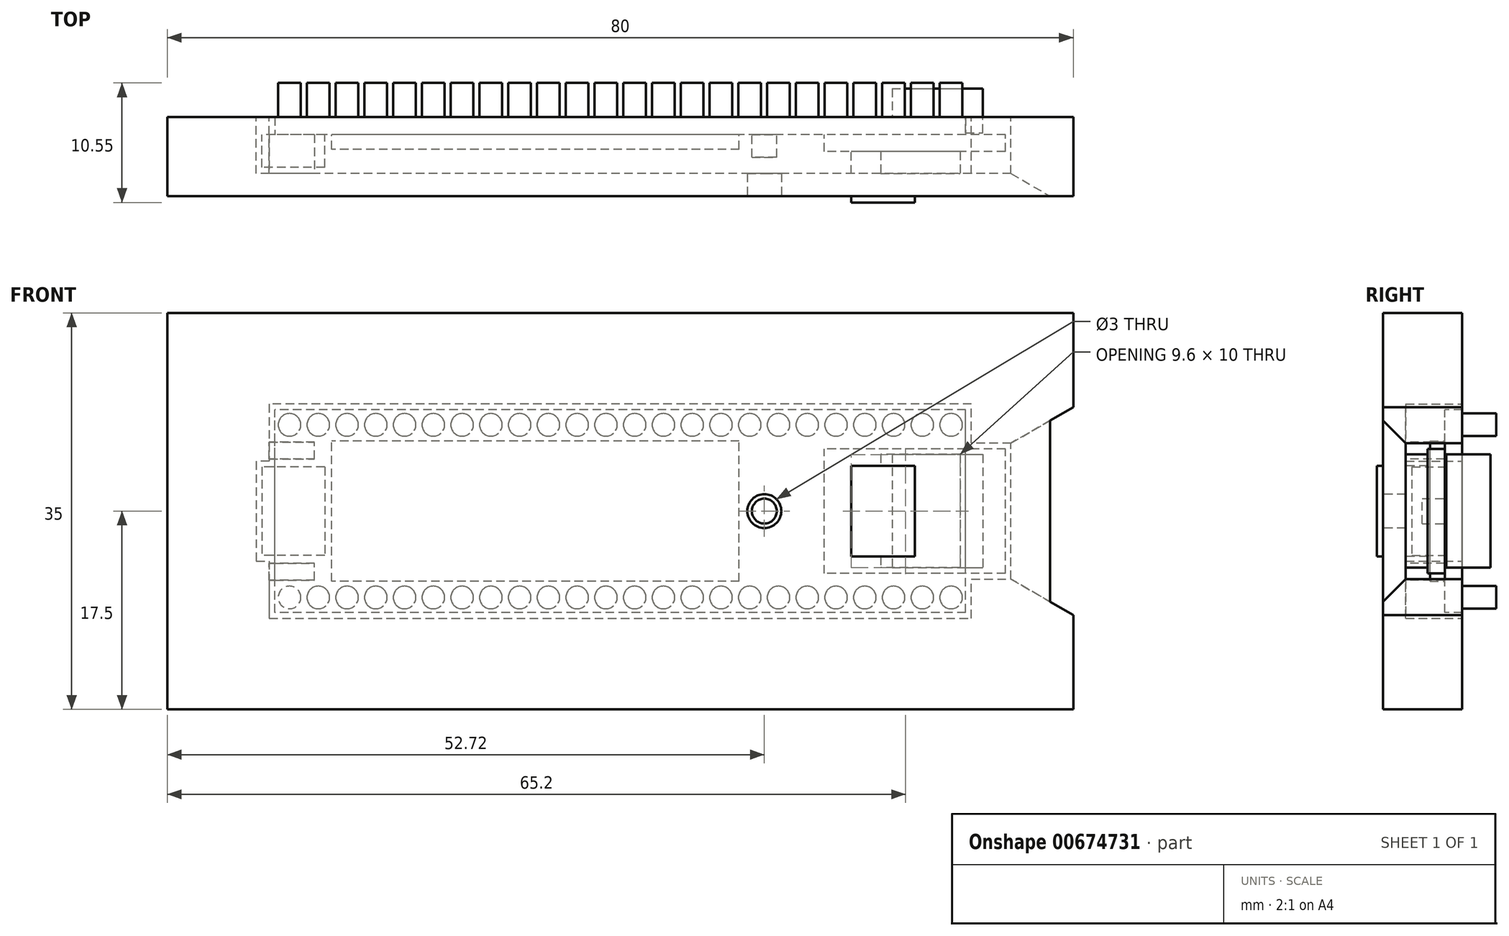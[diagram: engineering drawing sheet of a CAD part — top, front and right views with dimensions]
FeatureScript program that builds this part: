
annotation { "Feature Type Name" : "Feature", "Feature Type Description" : "" }
export const myFeature = defineFeature(function(context is Context, id is Id, definition is map)
    precondition{}
    {
        {
            var Q0;
            Q0=qCreatedBy(makeId("Front.planeOp"),FACE);
            var sketch = newSketch(context, id + "F0", { "sketchPlane" : qUnion([Q0])});
            skLineSegment(sketch, "E0.bottom", {"start": v(30.5, -8.95) * mm, "end": v(-30.5, -8.95) * mm});
            skLineSegment(sketch, "E0.top", {"start": v(30.5, 8.95) * mm, "end": v(-30.5, 8.95) * mm});
            skLineSegment(sketch, "E0.left", {"start": v(30.5, -8.95) * mm, "end": v(30.5, 8.95) * mm});
            skLineSegment(sketch, "E0.right", {"start": v(-30.5, -8.95) * mm, "end": v(-30.5, 8.95) * mm});
            skPoint(sketch, "E0.middle", {"position": v(0, 0) * mm});
            skCircle(sketch, "E1", {"center": v(12.72, 0) * mm, "radius": 1.1 * mm});
            skLineSegment(sketch, "E2.bottom", {"start": v(34, -5.5) * mm, "end": v(18, -5.5) * mm});
            skLineSegment(sketch, "E2.top", {"start": v(34, 5.5) * mm, "end": v(18, 5.5) * mm});
            skLineSegment(sketch, "E2.left", {"start": v(34, -5.5) * mm, "end": v(34, 5.5) * mm});
            skLineSegment(sketch, "E2.right", {"start": v(18, -5.5) * mm, "end": v(18, 5.5) * mm});
            skPoint(sketch, "E2.middle", {"position": v(26, 0) * mm});
            skLineSegment(sketch, "E3.bottom", {"start": v(-26.1, 3.9) * mm, "end": v(-31.65, 3.9) * mm});
            skLineSegment(sketch, "E3.top", {"start": v(-26.1, -3.9) * mm, "end": v(-31.65, -3.9) * mm});
            skLineSegment(sketch, "E3.left", {"start": v(-26.1, 3.9) * mm, "end": v(-26.1, -3.9) * mm});
            skLineSegment(sketch, "E3.right", {"start": v(-31.65, 3.9) * mm, "end": v(-31.65, -3.9) * mm});
            skPoint(sketch, "E3.middle", {"position": v(-28.87, 0) * mm});
            skLineSegment(sketch, "E4.bottom", {"start": v(10.5, -6.2) * mm, "end": v(-25.5, -6.2) * mm});
            skLineSegment(sketch, "E4.top", {"start": v(10.5, 6.2) * mm, "end": v(-25.5, 6.2) * mm});
            skLineSegment(sketch, "E4.left", {"start": v(10.5, -6.2) * mm, "end": v(10.5, 6.2) * mm});
            skLineSegment(sketch, "E4.right", {"start": v(-25.5, -6.2) * mm, "end": v(-25.5, 6.2) * mm});
            skPoint(sketch, "E4.middle", {"position": v(-7.5, 0) * mm});
            skSolve(sketch);
        }
        {
            var Q0;
            {var subQ8=sQuery(id+"F0.wireOp",EDGE,"E0.bottom");Q0=makeQuery(id+"F0.imprint","IMPRINT",FACE,{"disambiguationData":[TD([[makeQuery(id+"F0.imprint","IMPRINT",EDGE,{"derivedFrom":subQ8}),-1.0]])]});}
            var Q1;
            {var subQ5=sQuery(id+"F0.wireOp",EDGE,"E3.left");Q1=makeQuery(id+"F0.imprint","IMPRINT",FACE,{"disambiguationData":[TD([[makeQuery(id+"F0.imprint","IMPRINT",EDGE,{"derivedFrom":subQ5}),-1.0]])]});}
            var Q2;
            {var subQ5=sQuery(id+"F0.wireOp",EDGE,"E2.right");Q2=makeQuery(id+"F0.imprint","IMPRINT",FACE,{"disambiguationData":[TD([[makeQuery(id+"F0.imprint","IMPRINT",EDGE,{"derivedFrom":subQ5}),-1.0]])]});}
            var Q3;
            Q3=makeQuery(id+"F0.imprint","IMPRINT",FACE,{"disambiguationData":[TD([[makeQuery(id+"F0.imprint","IMPRINT",EDGE,{"derivedFrom":sQuery(id+"F0.wireOp",EDGE,"E1")}),1.0]])]});
            var Q4;
            Q4=makeQuery(id+"F0.imprint","IMPRINT",FACE,{"disambiguationData":[TD([[makeQuery(id+"F0.imprint","IMPRINT",EDGE,{"derivedFrom":sQuery(id+"F0.wireOp",EDGE,"E4.bottom")}),-1.0]])]});
            extrude(context, id + "F1", {"entities" : qUnion([Q0, Q1, Q2, Q3, Q4]), "oppositeDirection" : true, "depth" : 1.55 * mm, "offsetDistance" : 25 * mm});
        }
        {
            var Q0;
            Q0=makeQuery(id+"F0.imprint","IMPRINT",FACE,{"disambiguationData":[TD([[makeQuery(id+"F0.imprint","IMPRINT",EDGE,{"derivedFrom":sQuery(id+"F0.wireOp",EDGE,"E1")}),1.0]])]});
            extrude(context, id + "F2", {"entities" : qUnion([Q0]), "operationType" : NewBodyOperationType.ADD, "depth" : 2 * mm, "offsetDistance" : 25 * mm});
        }
        {
            var Q0;
            {var subQ5=sQuery(id+"F0.wireOp",EDGE,"E3.left");Q0=makeQuery(id+"F0.imprint","IMPRINT",FACE,{"disambiguationData":[TD([[makeQuery(id+"F0.imprint","IMPRINT",EDGE,{"derivedFrom":subQ5}),-1.0]])]});}
            var Q1;
            {var subQ5=sQuery(id+"F0.wireOp",EDGE,"E3.right");Q1=makeQuery(id+"F0.imprint","IMPRINT",FACE,{"disambiguationData":[TD([[makeQuery(id+"F0.imprint","IMPRINT",EDGE,{"derivedFrom":subQ5}),1.0]])]});}
            extrude(context, id + "F3", {"entities" : qUnion([Q0, Q1]), "operationType" : NewBodyOperationType.ADD, "depth" : 2.9 * mm, "offsetDistance" : 25 * mm});
        }
        {
            var Q0;
            {var subQ5=sQuery(id+"F0.wireOp",EDGE,"E2.left");Q0=makeQuery(id+"F0.imprint","IMPRINT",FACE,{"disambiguationData":[TD([[makeQuery(id+"F0.imprint","IMPRINT",EDGE,{"derivedFrom":subQ5}),1.0]])]});}
            var Q1;
            {var subQ5=sQuery(id+"F0.wireOp",EDGE,"E2.right");Q1=makeQuery(id+"F0.imprint","IMPRINT",FACE,{"disambiguationData":[TD([[makeQuery(id+"F0.imprint","IMPRINT",EDGE,{"derivedFrom":subQ5}),-1.0]])]});}
            extrude(context, id + "F4", {"entities" : qUnion([Q0, Q1]), "operationType" : NewBodyOperationType.ADD, "depth" : 1.5 * mm, "offsetDistance" : 25 * mm});
        }
        {
            var Q0;
            Q0=makeQuery(id+"F0.imprint","IMPRINT",FACE,{"disambiguationData":[TD([[makeQuery(id+"F0.imprint","IMPRINT",EDGE,{"derivedFrom":sQuery(id+"F0.wireOp",EDGE,"E4.bottom")}),-1.0]])]});
            extrude(context, id + "F5", {"entities" : qUnion([Q0]), "operationType" : NewBodyOperationType.ADD, "depth" : 1.3 * mm, "offsetDistance" : 25 * mm});
        }
        {
            var Q0;
            Q0=makeQuery(id+"F1.opExtrude","CAP_FACE",FACE,{"disambiguationData":[OSD([sQuery(id+"F0.wireOp",EDGE,"E0.bottom"),sQuery(id+"F0.wireOp",EDGE,"E0.top"),sQuery(id+"F0.wireOp",EDGE,"E0.left"),sQuery(id+"F0.wireOp",EDGE,"E0.right")])],"isStart":false});
            var sketch = newSketch(context, id + "F6", { "sketchPlane" : qUnion([Q0])});
            skCircle(sketch, "E5", {"center": v(29.21, -7.62) * mm, "radius": 1 * mm});
            skCircle(sketch, "E6.0.1.0", {"center": v(29.21, 7.62) * mm, "radius": 1 * mm});
            skCircle(sketch, "E6.1.0.0", {"center": v(26.67, -7.62) * mm, "radius": 1 * mm});
            skCircle(sketch, "E6.1.1.0", {"center": v(26.67, 7.62) * mm, "radius": 1 * mm});
            skCircle(sketch, "E6.2.0.0", {"center": v(24.13, -7.62) * mm, "radius": 1 * mm});
            skCircle(sketch, "E6.2.1.0", {"center": v(24.13, 7.62) * mm, "radius": 1 * mm});
            skCircle(sketch, "E6.3.0.0", {"center": v(21.6, -7.62) * mm, "radius": 1 * mm});
            skCircle(sketch, "E6.3.1.0", {"center": v(21.6, 7.62) * mm, "radius": 1 * mm});
            skCircle(sketch, "E6.4.0.0", {"center": v(19.05, -7.62) * mm, "radius": 1 * mm});
            skCircle(sketch, "E6.4.1.0", {"center": v(19.05, 7.62) * mm, "radius": 1 * mm});
            skCircle(sketch, "E6.5.0.0", {"center": v(16.51, -7.62) * mm, "radius": 1 * mm});
            skCircle(sketch, "E6.5.1.0", {"center": v(16.51, 7.62) * mm, "radius": 1 * mm});
            skCircle(sketch, "E6.6.0.0", {"center": v(13.97, -7.62) * mm, "radius": 1 * mm});
            skCircle(sketch, "E6.6.1.0", {"center": v(13.97, 7.62) * mm, "radius": 1 * mm});
            skCircle(sketch, "E6.7.0.0", {"center": v(11.43, -7.62) * mm, "radius": 1 * mm});
            skCircle(sketch, "E6.7.1.0", {"center": v(11.43, 7.62) * mm, "radius": 1 * mm});
            skCircle(sketch, "E6.8.0.0", {"center": v(8.9, -7.62) * mm, "radius": 1 * mm});
            skCircle(sketch, "E6.8.1.0", {"center": v(8.9, 7.62) * mm, "radius": 1 * mm});
            skCircle(sketch, "E6.9.0.0", {"center": v(6.35, -7.62) * mm, "radius": 1 * mm});
            skCircle(sketch, "E6.9.1.0", {"center": v(6.35, 7.62) * mm, "radius": 1 * mm});
            skCircle(sketch, "E6.10.0.0", {"center": v(3.81, -7.62) * mm, "radius": 1 * mm});
            skCircle(sketch, "E6.10.1.0", {"center": v(3.81, 7.62) * mm, "radius": 1 * mm});
            skCircle(sketch, "E6.11.0.0", {"center": v(1.27, -7.62) * mm, "radius": 1 * mm});
            skCircle(sketch, "E6.11.1.0", {"center": v(1.27, 7.62) * mm, "radius": 1 * mm});
            skCircle(sketch, "E6.12.0.0", {"center": v(-1.27, -7.62) * mm, "radius": 1 * mm});
            skCircle(sketch, "E6.12.1.0", {"center": v(-1.27, 7.62) * mm, "radius": 1 * mm});
            skCircle(sketch, "E6.13.0.0", {"center": v(-3.81, -7.62) * mm, "radius": 1 * mm});
            skCircle(sketch, "E6.13.1.0", {"center": v(-3.81, 7.62) * mm, "radius": 1 * mm});
            skCircle(sketch, "E6.14.0.0", {"center": v(-6.35, -7.62) * mm, "radius": 1 * mm});
            skCircle(sketch, "E6.14.1.0", {"center": v(-6.35, 7.62) * mm, "radius": 1 * mm});
            skCircle(sketch, "E6.15.0.0", {"center": v(-8.9, -7.62) * mm, "radius": 1 * mm});
            skCircle(sketch, "E6.15.1.0", {"center": v(-8.9, 7.62) * mm, "radius": 1 * mm});
            skCircle(sketch, "E6.16.0.0", {"center": v(-11.43, -7.62) * mm, "radius": 1 * mm});
            skCircle(sketch, "E6.16.1.0", {"center": v(-11.43, 7.62) * mm, "radius": 1 * mm});
            skCircle(sketch, "E6.17.0.0", {"center": v(-13.97, -7.62) * mm, "radius": 1 * mm});
            skCircle(sketch, "E6.17.1.0", {"center": v(-13.97, 7.62) * mm, "radius": 1 * mm});
            skCircle(sketch, "E6.18.0.0", {"center": v(-16.51, -7.62) * mm, "radius": 1 * mm});
            skCircle(sketch, "E6.18.1.0", {"center": v(-16.51, 7.62) * mm, "radius": 1 * mm});
            skCircle(sketch, "E6.19.0.0", {"center": v(-19.05, -7.62) * mm, "radius": 1 * mm});
            skCircle(sketch, "E6.19.1.0", {"center": v(-19.05, 7.62) * mm, "radius": 1 * mm});
            skCircle(sketch, "E6.20.0.0", {"center": v(-21.6, -7.62) * mm, "radius": 1 * mm});
            skCircle(sketch, "E6.20.1.0", {"center": v(-21.6, 7.62) * mm, "radius": 1 * mm});
            skCircle(sketch, "E6.21.0.0", {"center": v(-24.13, -7.62) * mm, "radius": 1 * mm});
            skCircle(sketch, "E6.21.1.0", {"center": v(-24.13, 7.62) * mm, "radius": 1 * mm});
            skCircle(sketch, "E6.22.0.0", {"center": v(-26.67, -7.62) * mm, "radius": 1 * mm});
            skCircle(sketch, "E6.22.1.0", {"center": v(-26.67, 7.62) * mm, "radius": 1 * mm});
            skCircle(sketch, "E6.23.0.0", {"center": v(-29.21, -7.62) * mm, "radius": 1 * mm});
            skCircle(sketch, "E6.23.1.0", {"center": v(-29.21, 7.62) * mm, "radius": 1 * mm});
            skLineSegment(sketch, "E6.direction1", {"start": v(29.21, -7.62) * mm, "end": v(26.67, -7.62) * mm, "construction": true});
            skLineSegment(sketch, "E6.direction2", {"start": v(29.21, -7.62) * mm, "end": v(29.21, 7.62) * mm, "construction": true});
            skSolve(sketch);
        }
        {
            var Q0;
            Q0 = qSketchRegion(id + "F6", true);
            extrude(context, id + "F7", {"entities" : qUnion([Q0]), "operationType" : NewBodyOperationType.ADD, "depth" : 3 * mm, "offsetDistance" : 25 * mm});
        }
        {
            var Q0;
            Q0=makeQuery(id+"F4.opExtrude","CAP_FACE",FACE,{"disambiguationData":[OSD([sQuery(id+"F0.wireOp",EDGE,"E2.bottom"),sQuery(id+"F0.wireOp",EDGE,"E2.top"),sQuery(id+"F0.wireOp",EDGE,"E2.left"),sQuery(id+"F0.wireOp",EDGE,"E2.right")])],"isStart":false});
            var sketch = newSketch(context, id + "F8", { "sketchPlane" : qUnion([Q0])});
            skLineSegment(sketch, "E7.bottom", {"start": v(26, -4) * mm, "end": v(20.4, -4) * mm});
            skLineSegment(sketch, "E7.top", {"start": v(26, 4) * mm, "end": v(20.4, 4) * mm});
            skLineSegment(sketch, "E7.left", {"start": v(26, -4) * mm, "end": v(26, 4) * mm});
            skLineSegment(sketch, "E7.right", {"start": v(20.4, -4) * mm, "end": v(20.4, 4) * mm});
            skPoint(sketch, "E7.middle", {"position": v(23.2, 0) * mm});
            skSolve(sketch);
        }
        {
            var Q0;
            Q0=makeQuery(id+"F1.opExtrude","CAP_FACE",FACE,{"disambiguationData":[OSD([sQuery(id+"F0.wireOp",EDGE,"E0.bottom"),sQuery(id+"F0.wireOp",EDGE,"E0.top"),sQuery(id+"F0.wireOp",EDGE,"E0.left"),sQuery(id+"F0.wireOp",EDGE,"E0.right")])],"isStart":false});
            var sketch = newSketch(context, id + "F9", { "sketchPlane" : qUnion([Q0])});
            skLineSegment(sketch, "E8.bottom", {"start": v(-24, 5) * mm, "end": v(-32, 5) * mm});
            skLineSegment(sketch, "E8.top", {"start": v(-24, -5) * mm, "end": v(-32, -5) * mm});
            skLineSegment(sketch, "E8.left", {"start": v(-24, 5) * mm, "end": v(-24, -5) * mm});
            skLineSegment(sketch, "E8.right", {"start": v(-32, 5) * mm, "end": v(-32, -5) * mm});
            skPoint(sketch, "E8.middle", {"position": v(-28, 0) * mm});
            skLineSegment(sketch, "E9", {"start": v(-30.5, -5) * mm, "end": v(-30.5, 5) * mm});
            skSolve(sketch);
        }
        {
            var Q0;
            Q0=makeQuery(id+"F8.imprint","IMPRINT",FACE,{"disambiguationData":[TD([[makeQuery(id+"F8.imprint","IMPRINT",EDGE,{"derivedFrom":sQuery(id+"F8.wireOp",EDGE,"E7.bottom")}),-1.0]])]});
            extrude(context, id + "F10", {"entities" : qUnion([Q0]), "depth" : 4.5 * mm, "offsetDistance" : 25 * mm});
        }
        {
            var Q0;
            {var subQ0=sQuery(id+"F9.wireOp",EDGE,"E8.right");Q0=makeQuery(id+"F9.imprint","IMPRINT",FACE,{"disambiguationData":[TD([[makeQuery(id+"F9.imprint","IMPRINT",EDGE,{"derivedFrom":subQ0}),1.0]])]});}
            extrude(context, id + "F11", {"entities" : qUnion([Q0]), "oppositeDirection" : true, "depth" : 1.4 * mm, "offsetDistance" : 25 * mm});
        }
        {
            var Q0;
            {var subQ0=sQuery(id+"F9.wireOp",EDGE,"E8.right");Q0=makeQuery(id+"F9.imprint","IMPRINT",FACE,{"disambiguationData":[TD([[makeQuery(id+"F9.imprint","IMPRINT",EDGE,{"derivedFrom":subQ0}),1.0]])]});}
            var Q1;
            {var subQ0=sQuery(id+"F9.wireOp",EDGE,"E8.left");Q1=makeQuery(id+"F9.imprint","IMPRINT",FACE,{"disambiguationData":[TD([[makeQuery(id+"F9.imprint","IMPRINT",EDGE,{"derivedFrom":subQ0}),-1.0]])]});}
            extrude(context, id + "F12", {"entities" : qUnion([Q0, Q1]), "operationType" : NewBodyOperationType.ADD, "depth" : 2.5 * mm, "offsetDistance" : 25 * mm});
        }
        {
            var Q0;
            {var subQ1=sQuery(id+"F9.wireOp",EDGE,"E8.left");Q0=makeQuery(id+"F9.imprint","IMPRINT",FACE,{"disambiguationData":[TD([[makeQuery(id+"F9.imprint","IMPRINT",EDGE,{"derivedFrom":subQ1}),1.0]])]});}
            var sketch = newSketch(context, id + "F13", { "sketchPlane" : qUnion([Q0])});
            skLineSegment(sketch, "E10.bottom", {"start": v(-40, -17.5) * mm, "end": v(40, -17.5) * mm});
            skLineSegment(sketch, "E10.top", {"start": v(-40, 17.5) * mm, "end": v(40, 17.5) * mm});
            skLineSegment(sketch, "E10.left", {"start": v(-40, -17.5) * mm, "end": v(-40, 17.5) * mm});
            skLineSegment(sketch, "E10.right", {"start": v(40, -17.5) * mm, "end": v(40, 17.5) * mm});
            skPoint(sketch, "E10.middle", {"position": v(0, 0) * mm});
            skLineSegment(sketch, "E11", {"start": v(30.5, 8.95) * mm, "end": v(30.5, 3.9) * mm, "construction": true});
            skLineSegment(sketch, "E12", {"start": v(30.5, 3.9) * mm, "end": v(31.65, 3.9) * mm, "construction": true});
            skLineSegment(sketch, "E13", {"start": v(31.65, 3.9) * mm, "end": v(31.65, -3.9) * mm, "construction": true});
            skLineSegment(sketch, "E14", {"start": v(31.65, -3.9) * mm, "end": v(30.5, -3.9) * mm, "construction": true});
            skLineSegment(sketch, "E15", {"start": v(30.5, -3.9) * mm, "end": v(30.5, -8.95) * mm, "construction": true});
            skLineSegment(sketch, "E16", {"start": v(30.5, -8.95) * mm, "end": v(-30.5, -8.95) * mm, "construction": true});
            skLineSegment(sketch, "E17", {"start": v(-30.5, -8.95) * mm, "end": v(-30.5, -5.5) * mm, "construction": true});
            skLineSegment(sketch, "E18", {"start": v(-30.5, -5.5) * mm, "end": v(-34, -5.5) * mm, "construction": true});
            skLineSegment(sketch, "E19", {"start": v(-34, -5.5) * mm, "end": v(-34, 5.5) * mm, "construction": true});
            skLineSegment(sketch, "E20", {"start": v(-34, 5.5) * mm, "end": v(-30.5, 5.5) * mm, "construction": true});
            skLineSegment(sketch, "E21", {"start": v(-30.5, 5.5) * mm, "end": v(-30.5, 8.95) * mm, "construction": true});
            skLineSegment(sketch, "E22", {"start": v(-30.5, 8.95) * mm, "end": v(30.5, 8.95) * mm, "construction": true});
            skLineSegment(sketch, "E23.0", {"start": v(-31, 6) * mm, "end": v(-31, 9.45) * mm});
            skLineSegment(sketch, "E23.1", {"start": v(32.15, -4.4) * mm, "end": v(31, -4.4) * mm});
            skLineSegment(sketch, "E23.2", {"start": v(32.15, 4.4) * mm, "end": v(32.15, -4.4) * mm});
            skLineSegment(sketch, "E23.3", {"start": v(31, 4.4) * mm, "end": v(32.15, 4.4) * mm});
            skLineSegment(sketch, "E23.4", {"start": v(31, 9.45) * mm, "end": v(31, 4.4) * mm});
            skLineSegment(sketch, "E23.5", {"start": v(31, -4.4) * mm, "end": v(31, -9.45) * mm});
            skLineSegment(sketch, "E23.6", {"start": v(-31, 9.45) * mm, "end": v(31, 9.45) * mm});
            skLineSegment(sketch, "E23.7", {"start": v(31, -9.45) * mm, "end": v(-31, -9.45) * mm});
            skLineSegment(sketch, "E23.8", {"start": v(-31, -9.45) * mm, "end": v(-31, -6) * mm});
            skLineSegment(sketch, "E23.9", {"start": v(-31, -6) * mm, "end": v(-34.5, -6) * mm});
            skLineSegment(sketch, "E23.10", {"start": v(-34.5, -6) * mm, "end": v(-34.5, 6) * mm});
            skLineSegment(sketch, "E23.11", {"start": v(-34.5, 6) * mm, "end": v(-31, 6) * mm});
            skLineSegment(sketch, "E24", {"start": v(31, 4.4) * mm, "end": v(31, -4.4) * mm});
            skLineSegment(sketch, "E25", {"start": v(-31, 6) * mm, "end": v(-31, -6) * mm});
            skLineSegment(sketch, "E26.bottom", {"start": v(27, 2.25) * mm, "end": v(29.5, 2.25) * mm});
            skLineSegment(sketch, "E26.top", {"start": v(27, -2.25) * mm, "end": v(29.5, -2.25) * mm});
            skLineSegment(sketch, "E26.left", {"start": v(27, 2.25) * mm, "end": v(27, -2.25) * mm});
            skLineSegment(sketch, "E26.right", {"start": v(29.5, 2.25) * mm, "end": v(29.5, -2.25) * mm});
            skPoint(sketch, "E26.middle", {"position": v(28.25, 0) * mm});
            skLineSegment(sketch, "E27.bottom", {"start": v(-25.25, -3.75) * mm, "end": v(-20.75, -3.75) * mm});
            skLineSegment(sketch, "E27.top", {"start": v(-25.25, 3.75) * mm, "end": v(-20.75, 3.75) * mm});
            skLineSegment(sketch, "E27.left", {"start": v(-25.25, -3.75) * mm, "end": v(-25.25, 3.75) * mm});
            skLineSegment(sketch, "E27.right", {"start": v(-20.75, -3.75) * mm, "end": v(-20.75, 3.75) * mm});
            skPoint(sketch, "E27.middle", {"position": v(-23, 0) * mm});
            skSolve(sketch);
        }
        {
            var Q0;
            Q0=makeQuery(id+"F13.imprint","IMPRINT",FACE,{"disambiguationData":[TD([[makeQuery(id+"F13.imprint","IMPRINT",EDGE,{"derivedFrom":sQuery(id+"F13.wireOp",EDGE,"E10.bottom")}),1.0]])]});
            extrude(context, id + "F14", {"entities" : qUnion([Q0]), "oppositeDirection" : true, "depth" : 7 * mm, "offsetDistance" : 25 * mm});
        }
        {
            var Q0;
            Q0=makeQuery(id+"F14.opExtrude","CAP_FACE",FACE,{"disambiguationData":[OSD([sQuery(id+"F13.wireOp",EDGE,"E10.bottom"),sQuery(id+"F13.wireOp",EDGE,"E10.top"),sQuery(id+"F13.wireOp",EDGE,"E10.left"),sQuery(id+"F13.wireOp",EDGE,"E10.right"),sQuery(id+"F13.wireOp",EDGE,"E23.0"),sQuery(id+"F13.wireOp",EDGE,"E23.1"),sQuery(id+"F13.wireOp",EDGE,"E23.2"),sQuery(id+"F13.wireOp",EDGE,"E23.3"),sQuery(id+"F13.wireOp",EDGE,"E23.4"),sQuery(id+"F13.wireOp",EDGE,"E23.5"),sQuery(id+"F13.wireOp",EDGE,"E23.6"),sQuery(id+"F13.wireOp",EDGE,"E23.7"),sQuery(id+"F13.wireOp",EDGE,"E23.8"),sQuery(id+"F13.wireOp",EDGE,"E23.9"),sQuery(id+"F13.wireOp",EDGE,"E23.10"),sQuery(id+"F13.wireOp",EDGE,"E23.11")])],"isStart":false});
            var sketch = newSketch(context, id + "F15", { "sketchPlane" : qUnion([Q0])});
            skLineSegment(sketch, "E28.bottom", {"start": v(-31, 6.1) * mm, "end": v(-27, 6.1) * mm});
            skLineSegment(sketch, "E28.top", {"start": v(-31, 4.6) * mm, "end": v(-27, 4.6) * mm});
            skLineSegment(sketch, "E28.left", {"start": v(-31, 6.1) * mm, "end": v(-31, 4.6) * mm});
            skLineSegment(sketch, "E28.right", {"start": v(-27, 6.1) * mm, "end": v(-27, 4.6) * mm});
            skLineSegment(sketch, "E29.bottom", {"start": v(-27, -4.6) * mm, "end": v(-31, -4.6) * mm});
            skLineSegment(sketch, "E29.top", {"start": v(-27, -6.1) * mm, "end": v(-31, -6.1) * mm});
            skLineSegment(sketch, "E29.left", {"start": v(-27, -4.6) * mm, "end": v(-27, -6.1) * mm});
            skLineSegment(sketch, "E29.right", {"start": v(-31, -4.6) * mm, "end": v(-31, -6.1) * mm});
            skLineSegment(sketch, "E30.bottom", {"start": v(23, -5) * mm, "end": v(30, -5) * mm});
            skLineSegment(sketch, "E30.top", {"start": v(23, 5) * mm, "end": v(30, 5) * mm});
            skLineSegment(sketch, "E30.left", {"start": v(23, -5) * mm, "end": v(23, 5) * mm});
            skLineSegment(sketch, "E30.right", {"start": v(30, -5) * mm, "end": v(30, 5) * mm});
            skPoint(sketch, "E30.middle", {"position": v(26.5, 0) * mm});
            skSolve(sketch);
        }
        {
            var Q0;
            Q0=makeQuery(id+"F15.imprint","IMPRINT",FACE,{"disambiguationData":[TD([[makeQuery(id+"F15.imprint","IMPRINT",EDGE,{"derivedFrom":makeQuery(id+"F14.opExtrude","CAP_EDGE",EDGE,{"disambiguationData":[OSD([sQuery(id+"F13.wireOp",EDGE,"E23.0")])],"isStart":false})}),1.0]])]});
            extrude(context, id + "F16", {"entities" : qUnion([Q0]), "operationType" : NewBodyOperationType.ADD, "oppositeDirection" : true, "depth" : 2 * mm, "offsetDistance" : 25 * mm});
        }
        {
            var Q0;
            Q0=makeQuery(id+"F15.imprint","IMPRINT",FACE,{"disambiguationData":[TD([[makeQuery(id+"F15.imprint","IMPRINT",EDGE,{"derivedFrom":sQuery(id+"F15.wireOp",EDGE,"E28.bottom")}),-1.0]])]});
            var Q1;
            Q1=makeQuery(id+"F15.imprint","IMPRINT",FACE,{"disambiguationData":[TD([[makeQuery(id+"F15.imprint","IMPRINT",EDGE,{"derivedFrom":sQuery(id+"F15.wireOp",EDGE,"E29.bottom")}),1.0]])]});
            var Q2;
            Q2=makeQuery(id+"F1.opExtrude","CAP_FACE",FACE,{"disambiguationData":[OSD([sQuery(id+"F0.wireOp",EDGE,"E0.bottom"),sQuery(id+"F0.wireOp",EDGE,"E0.top"),sQuery(id+"F0.wireOp",EDGE,"E0.left"),sQuery(id+"F0.wireOp",EDGE,"E0.right")])],"isStart":true});
            extrude(context, id + "F17", {"entities" : qUnion([Q0, Q1]), "operationType" : NewBodyOperationType.ADD, "endBound" : BoundingType.UP_TO_SURFACE, "oppositeDirection" : true, "depth" : 5 * mm, "endBoundEntityFace" : qUnion([Q2]), "offsetDistance" : 25 * mm});
        }
        {
            var Q0;
            Q0=makeQuery(id+"F15.imprint","IMPRINT",FACE,{"disambiguationData":[TD([[makeQuery(id+"F15.imprint","IMPRINT",EDGE,{"derivedFrom":sQuery(id+"F15.wireOp",EDGE,"E30.bottom")}),1.0]])]});
            var Q1;
            Q1=makeQuery(id+"F4.opExtrude","CAP_FACE",FACE,{"disambiguationData":[OSD([sQuery(id+"F0.wireOp",EDGE,"E2.bottom"),sQuery(id+"F0.wireOp",EDGE,"E2.top"),sQuery(id+"F0.wireOp",EDGE,"E2.left"),sQuery(id+"F0.wireOp",EDGE,"E2.right")])],"isStart":false});
            extrude(context, id + "F18", {"entities" : qUnion([Q0]), "operationType" : NewBodyOperationType.ADD, "endBound" : BoundingType.UP_TO_SURFACE, "oppositeDirection" : true, "depth" : 25 * mm, "endBoundEntityFace" : qUnion([Q1]), "offsetDistance" : 25 * mm});
        }
        {
            var Q0;
            {var subQ3=sQuery(id+"F15.wireOp",EDGE,"E28.left");Q0=makeQuery(id+"F15.imprint","IMPRINT",FACE,{"disambiguationData":[TD([[makeQuery(id+"F15.imprint","IMPRINT",EDGE,{"derivedFrom":subQ3}),-1.0]])]});}
            var sketch = newSketch(context, id + "F19", { "sketchPlane" : qUnion([Q0])});
            skCircle(sketch, "E31", {"center": v(12.72, 0) * mm, "radius": 1.5 * mm});
            skSolve(sketch);
        }
        {
            var Q0;
            Q0=makeQuery(id+"F19.imprint","IMPRINT",FACE,{"disambiguationData":[TD([[makeQuery(id+"F19.imprint","IMPRINT",EDGE,{"derivedFrom":sQuery(id+"F19.wireOp",EDGE,"E31")}),1.0]])]});
            extrude(context, id + "F20", {"entities" : qUnion([Q0]), "operationType" : NewBodyOperationType.REMOVE, "endBound" : BoundingType.UP_TO_NEXT, "oppositeDirection" : true, "depth" : 25 * mm, "offsetDistance" : 25 * mm});
        }
        {
            var Q0;
            Q0=makeQuery(id+"F14.opExtrude","SWEPT_FACE",FACE,{"disambiguationData":[OSD([sQuery(id+"F13.wireOp",EDGE,"E23.10")])]});
            var sketch = newSketch(context, id + "F21", { "sketchPlane" : qUnion([Q0])});
            skLineSegment(sketch, "E32.bottom", {"start": v(1.5, -5.5) * mm, "end": v(0, -5.5) * mm, "construction": true});
            skLineSegment(sketch, "E32.top", {"start": v(1.5, 5.5) * mm, "end": v(0, 5.5) * mm, "construction": true});
            skLineSegment(sketch, "E32.left", {"start": v(1.5, -5.5) * mm, "end": v(1.5, 5.5) * mm, "construction": true});
            skLineSegment(sketch, "E32.right", {"start": v(0, -5.5) * mm, "end": v(0, 5.5) * mm, "construction": true});
            skLineSegment(sketch, "E33.0", {"start": v(4.5, -8.5) * mm, "end": v(4.5, 8.5) * mm});
            skLineSegment(sketch, "E33.1", {"start": v(4.5, -8.5) * mm, "end": v(-3, -8.5) * mm});
            skLineSegment(sketch, "E33.2", {"start": v(-3, -8.5) * mm, "end": v(-3, 8.5) * mm});
            skLineSegment(sketch, "E33.3", {"start": v(4.5, 8.5) * mm, "end": v(-3, 8.5) * mm});
            skSolve(sketch);
        }
        {
            var Q0;
            {var subQ0=sQuery(id+"F13.wireOp",EDGE,"E23.10");Q0=makeQuery(id+"F21.imprint","IMPRINT",FACE,{"disambiguationData":[TD([[makeQuery(id+"F21.imprint","IMPRINT",EDGE,{"derivedFrom":makeQuery(id+"F14.opExtrude","CAP_EDGE",EDGE,{"disambiguationData":[OSD([subQ0])],"isStart":true})}),-1.0]])]});}
            var Q1;
            Q1=makeQuery(id+"F14.opExtrude","SWEPT_FACE",FACE,{"disambiguationData":[OSD([sQuery(id+"F13.wireOp",EDGE,"E10.left")])]});
            extrude(context, id + "F22", {"entities" : qUnion([Q0]), "operationType" : NewBodyOperationType.REMOVE, "endBound" : BoundingType.UP_TO_SURFACE, "oppositeDirection" : true, "depth" : 25 * mm, "endBoundEntityFace" : qUnion([Q1]), "offsetDistance" : 25 * mm, "hasDraft" : true, "draftAngle" : 30 * degree});
        }
    });
